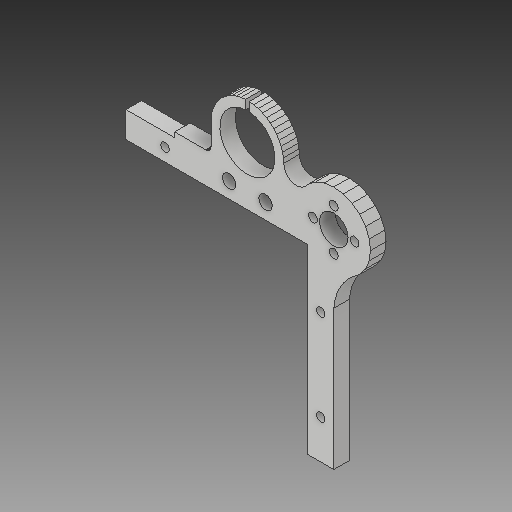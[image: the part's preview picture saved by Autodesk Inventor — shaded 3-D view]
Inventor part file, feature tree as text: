
AUTODESK INVENTOR PART (.ipt)
format: ipt  version: 2018 (Build 220112000, 112)  size: 296,960 bytes
history: native  units: mm
features: sketch x4, other x3
ambient origin geometry x8: Origin, YZ Plane, XZ Plane, XY Plane, X Axis, Y Axis, Z Axis, Center Point
bodies: Solid1 (feature_tree)
feature tree (7):
  other  "Left Bed Holder Mid.ipt"
  other  "Solid1::Left Bed Holder Mid.ipt"
  other  "TaggingFeature1"
  sketch  "Sketch1"  dims[d0=10.0mm]
  sketch  "Sketch2"
  sketch  "Sketch3"
  sketch  "Sketch4"
